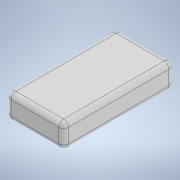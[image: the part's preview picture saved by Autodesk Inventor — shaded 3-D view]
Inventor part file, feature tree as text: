
AUTODESK INVENTOR PART (.ipt)
format: ipt  version: 2021 (Build 250183000, 183)  size: 119,808 bytes
history: native  units: mm
features: other x1, extrude x1, fillet x1, sketch x1
ambient origin geometry x8: Origin, YZ Plane, XZ Plane, XY Plane, X Axis, Y Axis, Z Axis, Center Point
bodies: Body1 (feature_tree)
feature tree (4):
  other  "Sólido1"
  extrude  "Extrusão1"  Depth=46.0mm
  fillet  "Arredondamento1"  Radius=10.0mm
  sketch  "Esboço1"  dims[d0=24.0mm d1=46.0mm d2=10.0mm d3=0.0mm d4=2.0mm]
